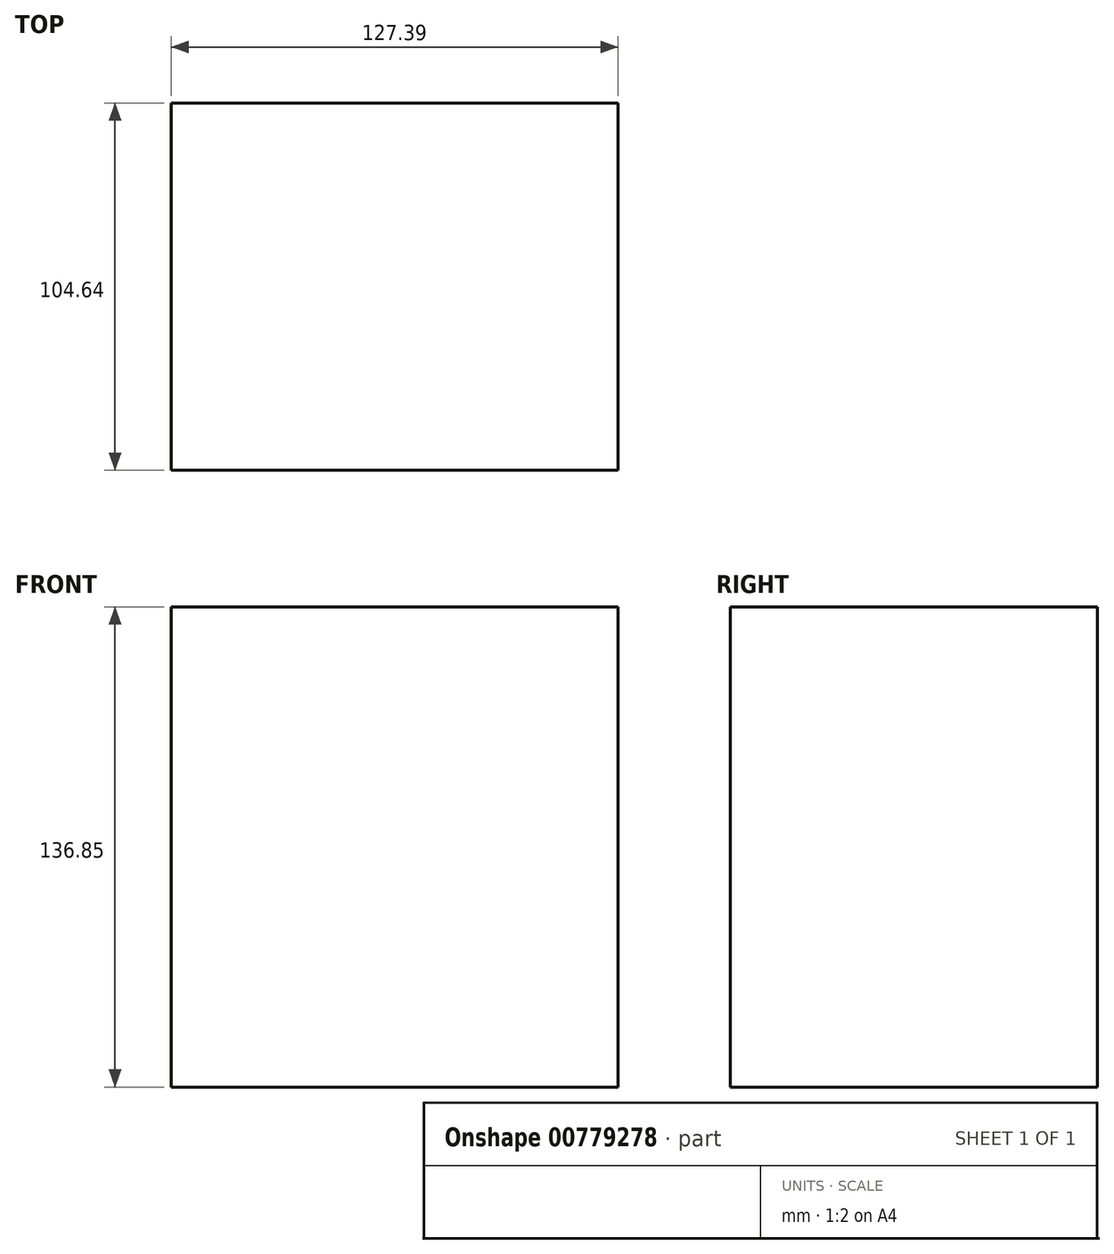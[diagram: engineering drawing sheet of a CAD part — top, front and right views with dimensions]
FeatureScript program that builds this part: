
annotation { "Feature Type Name" : "Feature", "Feature Type Description" : "" }
export const myFeature = defineFeature(function(context is Context, id is Id, definition is map)
    precondition{}
    {
        {
            var Q0;
            Q0=qCreatedBy(makeId("Top.planeOp"),FACE);
            var sketch = newSketch(context, id + "F0", { "sketchPlane" : qUnion([Q0])});
            skLineSegment(sketch, "E0.bottom", {"start": v(-1.86, 5.79) * mm, "end": v(-129.25, 5.79) * mm});
            skLineSegment(sketch, "E0.top", {"start": v(-1.86, 110.43) * mm, "end": v(-129.25, 110.43) * mm});
            skLineSegment(sketch, "E0.left", {"start": v(-1.86, 5.79) * mm, "end": v(-1.86, 110.43) * mm});
            skLineSegment(sketch, "E0.right", {"start": v(-129.25, 5.79) * mm, "end": v(-129.25, 110.43) * mm});
            skSolve(sketch);
        }
        {
            var Q0;
            Q0=makeQuery(id+"F0.imprint","IMPRINT",FACE,{"disambiguationData":[TD([[makeQuery(id+"F0.imprint","IMPRINT",EDGE,{"derivedFrom":sQuery(id+"F0.wireOp",EDGE,"E0.bottom")}),-1.0]])]});
            var Q1;
            Q1=sQuery(id+"F0.wireOp",EDGE,"E0.left");
            var Q2;
            Q2=sQuery(id+"F0.wireOp",EDGE,"E0.top");
            var Q3;
            Q3=sQuery(id+"F0.wireOp",EDGE,"E0.right");
            var Q4;
            Q4=sQuery(id+"F0.wireOp",EDGE,"E0.bottom");
            extrude(context, id + "F1", {"entities" : qUnion([Q0]), "surfaceEntities" : qUnion([Q1, Q2, Q3, Q4]), "depth" : 136.85 * mm, "offsetDistance" : 25.4 * mm});
        }
    });
